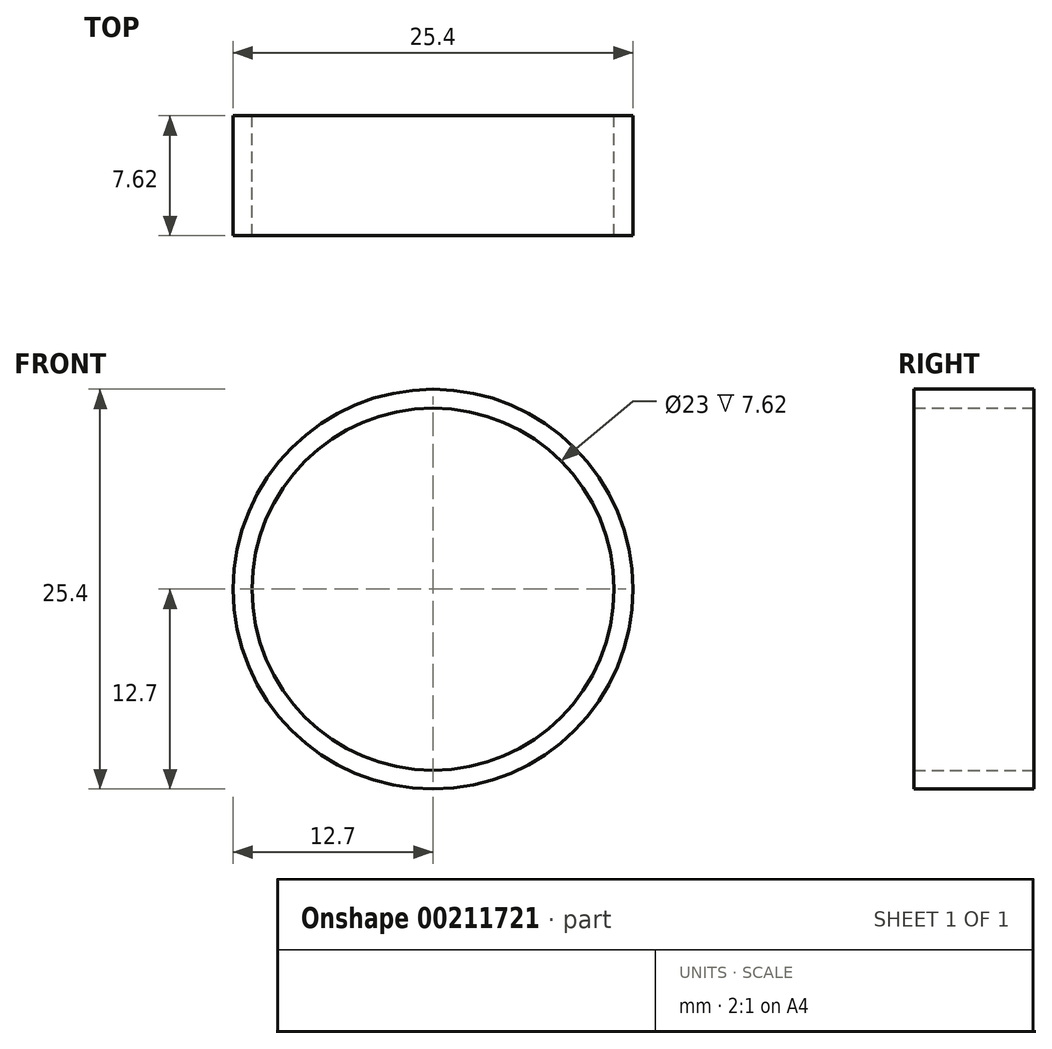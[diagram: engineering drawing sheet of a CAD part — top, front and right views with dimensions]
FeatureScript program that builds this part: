
annotation { "Feature Type Name" : "Feature", "Feature Type Description" : "" }
export const myFeature = defineFeature(function(context is Context, id is Id, definition is map)
    precondition{}
    {
        {
            var Q0;
            Q0=qCreatedBy(makeId("Front.planeOp"),FACE);
            var sketch = newSketch(context, id + "F0", { "sketchPlane" : qUnion([Q0])});
            skCircle(sketch, "E0", {"center": v(0, 0) * mm, "radius": 12.7 * mm});
            skCircle(sketch, "E1", {"center": v(0, 0) * mm, "radius": 11.5 * mm});
            skSolve(sketch);
        }
        {
            var Q0;
            Q0=makeQuery(id+"F0.imprint","IMPRINT",FACE,{"disambiguationData":[TD([[makeQuery(id+"F0.imprint","IMPRINT",EDGE,{"derivedFrom":sQuery(id+"F0.wireOp",EDGE,"E0")}),1.0]])]});
            extrude(context, id + "F3", {"entities" : qUnion([Q0]), "depth" : 7.62 * mm});
        }
    });
